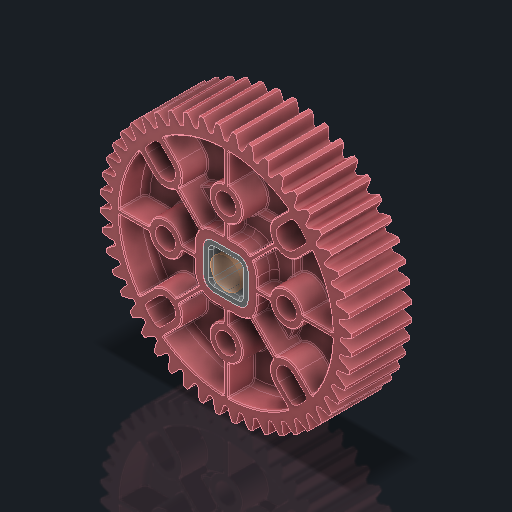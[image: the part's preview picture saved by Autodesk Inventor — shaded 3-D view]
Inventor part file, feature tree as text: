
AUTODESK INVENTOR PART (.ipt)
format: ipt  version: 2023.2 (Build 272271030, 271C)  size: 2,685,952 bytes
history: native  units: in
note: dims shown in document units (in); Inventor stores cm internally (conversion verified against a paired STEP export)
features: other x3, sketch x1, extrude x1
ambient origin geometry x8: Origin, YZ Plane, XZ Plane, XY Plane, X Axis, Y Axis, Z Axis, Center Point
bodies: Solid1 (feature_tree), Solid2 (feature_tree)
feature tree (5):
  sketch  "Sketch1"  dims[d0=0.25in d1=0.3937in d2=0.0in]
  other  "Srf1"
  other  "276-7573-001_OVERMOLD Rev7_48T 24DP Gear_1:1"
  other  "276-7573-002 Rev7_2:1"
  extrude  "ExtrusionSrf1"  Depth=0.3937in TaperAngle=0.0deg
